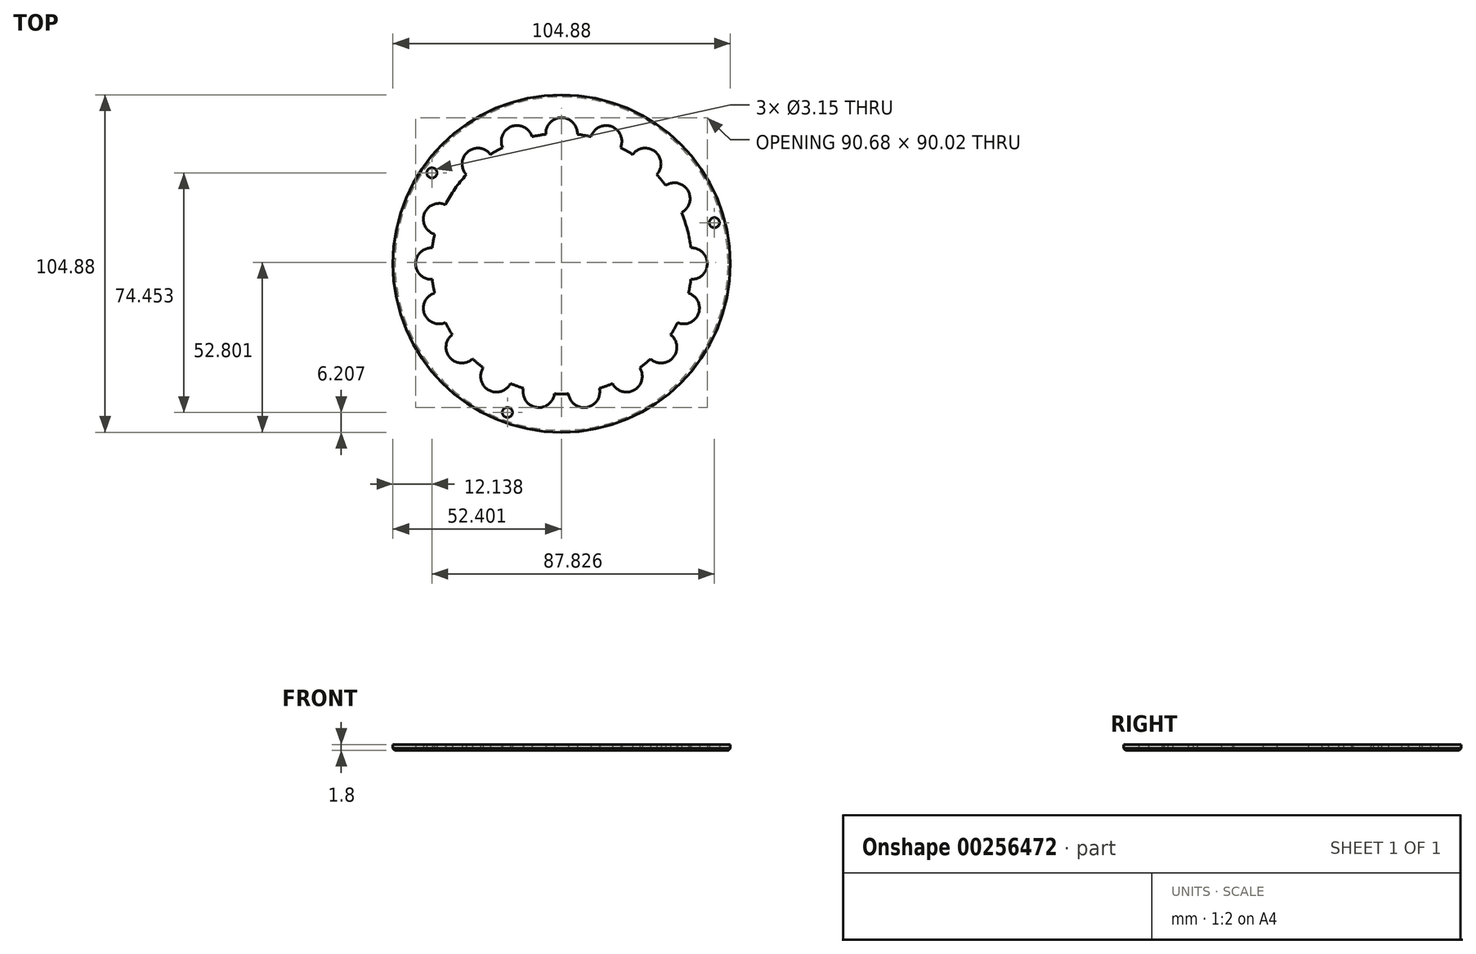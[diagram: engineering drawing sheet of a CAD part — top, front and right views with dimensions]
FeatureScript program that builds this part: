
annotation { "Feature Type Name" : "Feature", "Feature Type Description" : "" }
export const myFeature = defineFeature(function(context is Context, id is Id, definition is map)
    precondition{}
    {
        {
            var Q0;
            Q0=qCreatedBy(makeId("Top.planeOp"),FACE);
            var sketch = newSketch(context, id + "F0", { "sketchPlane" : qUnion([Q0])});
            skCircle(sketch, "E0", {"center": v(0, 0) * mm, "radius": 17.48 * mm});
            skCircle(sketch, "E1", {"center": v(0, 0) * mm, "radius": 13.5 * mm});
            skCircle(sketch, "E2", {"center": v(0, 0) * mm, "radius": 15.1 * mm, "construction": true});
            skCircle(sketch, "E3", {"center": v(13.47, 0) * mm, "radius": 1.63 * mm});
            skCircle(sketch, "E4.1.0", {"center": v(12.65, -4.61) * mm, "radius": 1.63 * mm});
            skCircle(sketch, "E4.2.0", {"center": v(10.31, -8.66) * mm, "radius": 1.63 * mm});
            skCircle(sketch, "E4.3.0", {"center": v(6.73, -11.67) * mm, "radius": 1.63 * mm});
            skCircle(sketch, "E4.4.0", {"center": v(2.33, -13.28) * mm, "radius": 1.63 * mm});
            skCircle(sketch, "E4.5.0", {"center": v(-2.35, -13.28) * mm, "radius": 1.63 * mm});
            skCircle(sketch, "E4.6.0", {"center": v(-6.75, -11.67) * mm, "radius": 1.63 * mm});
            skCircle(sketch, "E4.7.0", {"center": v(-10.34, -8.66) * mm, "radius": 1.63 * mm});
            skCircle(sketch, "E4.8.0", {"center": v(-12.68, -4.61) * mm, "radius": 1.63 * mm});
            skCircle(sketch, "E4.9.0", {"center": v(-13.5, 0) * mm, "radius": 1.63 * mm});
            skCircle(sketch, "E4.10.0", {"center": v(-12.68, 4.61) * mm, "radius": 1.63 * mm});
            skPoint(sketch, "E4.center", {"position": v(-0.01, 0) * mm});
            skLineSegment(sketch, "E4.anchor1", {"start": v(-0.01, 0) * mm, "end": v(13.47, 0) * mm, "construction": true});
            skLineSegment(sketch, "E4.anchor2", {"start": v(-0.01, 0) * mm, "end": v(-12.68, 4.61) * mm, "construction": true});
            skCircle(sketch, "E5.1.0", {"center": v(-8.67, 10.33) * mm, "radius": 1.63 * mm});
            skLineSegment(sketch, "E5.anchor1", {"start": v(0, 0) * mm, "end": v(-12.68, 4.61) * mm, "construction": true});
            skLineSegment(sketch, "E5.anchor2", {"start": v(0, 0) * mm, "end": v(-8.67, 10.33) * mm, "construction": true});
            skCircle(sketch, "E6.1.0", {"center": v(-4.61, 12.68) * mm, "radius": 1.63 * mm});
            skCircle(sketch, "E6.2.0", {"center": v(0, 13.5) * mm, "radius": 1.63 * mm});
            skCircle(sketch, "E6.3.0", {"center": v(4.61, 12.68) * mm, "radius": 1.63 * mm});
            skCircle(sketch, "E6.4.0", {"center": v(8.67, 10.33) * mm, "radius": 1.63 * mm});
            skCircle(sketch, "E6.5.0", {"center": v(11.68, 6.75) * mm, "radius": 1.63 * mm});
            skLineSegment(sketch, "E6.anchor2", {"start": v(0, 0) * mm, "end": v(11.68, 6.75) * mm, "construction": true});
            skCircle(sketch, "E7", {"center": v(0, 0) * mm, "radius": 16.4 * mm, "construction": true});
            skLineSegment(sketch, "E8", {"start": v(0, 0) * mm, "end": v(15.84, 4.24) * mm, "construction": true});
            skCircle(sketch, "E9", {"center": v(15.84, 4.24) * mm, "radius": 0.53 * mm});
            skLineSegment(sketch, "E10", {"start": v(0, 0) * mm, "end": v(-5.6, -15.41) * mm, "construction": true});
            skLineSegment(sketch, "E11", {"start": v(0, 0) * mm, "end": v(-13.43, 9.4) * mm, "construction": true});
            skCircle(sketch, "E12", {"center": v(-13.43, 9.4) * mm, "radius": 0.53 * mm});
            skCircle(sketch, "E13", {"center": v(-5.6, -15.41) * mm, "radius": 0.53 * mm});
            skSolve(sketch);
        }
        {
            var Q0;
            Q0=makeQuery(id+"F0.imprint","IMPRINT",FACE,{"disambiguationData":[TD([[makeQuery(id+"F0.imprint","IMPRINT",EDGE,{"derivedFrom":sQuery(id+"F0.wireOp",EDGE,"E0")}),1.0]])]});
            extrude(context, id + "F1", {"entities" : qUnion([Q0]), "depth" : 0.6 * mm});
        }
        {
            var Q0;
            Q0=makeQuery(id+"F1.opExtrude","CAP_EDGE",EDGE,{"disambiguationData":[OSD([sQuery(id+"F0.wireOp",EDGE,"E0")])],"isStart":true});
            chamfer(context, id + "F2", {"entities" : qUnion([Q0]), "width" : 0.2 * mm, "tangentPropagation" : true});
        }
        {
            var Q0;
            Q0=makeQuery(id+"F1.opExtrude","SWEPT_BODY",BODY,{"disambiguationData":[OSD([sQuery(id+"F0.wireOp",EDGE,"E0"),sQuery(id+"F0.wireOp",EDGE,"E1"),sQuery(id+"F0.wireOp",EDGE,"E3"),sQuery(id+"F0.wireOp",EDGE,"E4.1.0"),sQuery(id+"F0.wireOp",EDGE,"E4.2.0"),sQuery(id+"F0.wireOp",EDGE,"E4.3.0"),sQuery(id+"F0.wireOp",EDGE,"E4.4.0"),sQuery(id+"F0.wireOp",EDGE,"E4.5.0"),sQuery(id+"F0.wireOp",EDGE,"E4.6.0"),sQuery(id+"F0.wireOp",EDGE,"E4.7.0"),sQuery(id+"F0.wireOp",EDGE,"E4.8.0"),sQuery(id+"F0.wireOp",EDGE,"E4.9.0"),sQuery(id+"F0.wireOp",EDGE,"E4.10.0"),sQuery(id+"F0.wireOp",EDGE,"E5.1.0"),sQuery(id+"F0.wireOp",EDGE,"E6.1.0"),sQuery(id+"F0.wireOp",EDGE,"E6.2.0"),sQuery(id+"F0.wireOp",EDGE,"E6.3.0"),sQuery(id+"F0.wireOp",EDGE,"E6.4.0"),sQuery(id+"F0.wireOp",EDGE,"E6.5.0"),sQuery(id+"F0.wireOp",EDGE,"E9"),sQuery(id+"F0.wireOp",EDGE,"E12"),sQuery(id+"F0.wireOp",EDGE,"E13")])]});
            var Q1;
            Q1=qCreatedBy(makeId("Origin.pointOp"),VERTEX);
            transform(context, id + "F3", {"entities" : qUnion([Q0]), "transformType" : TransformType.SCALE_UNIFORMLY, "scale" : 3, "makeCopy" : false, "scalePoint" : qUnion([Q1])});
        }
    });
